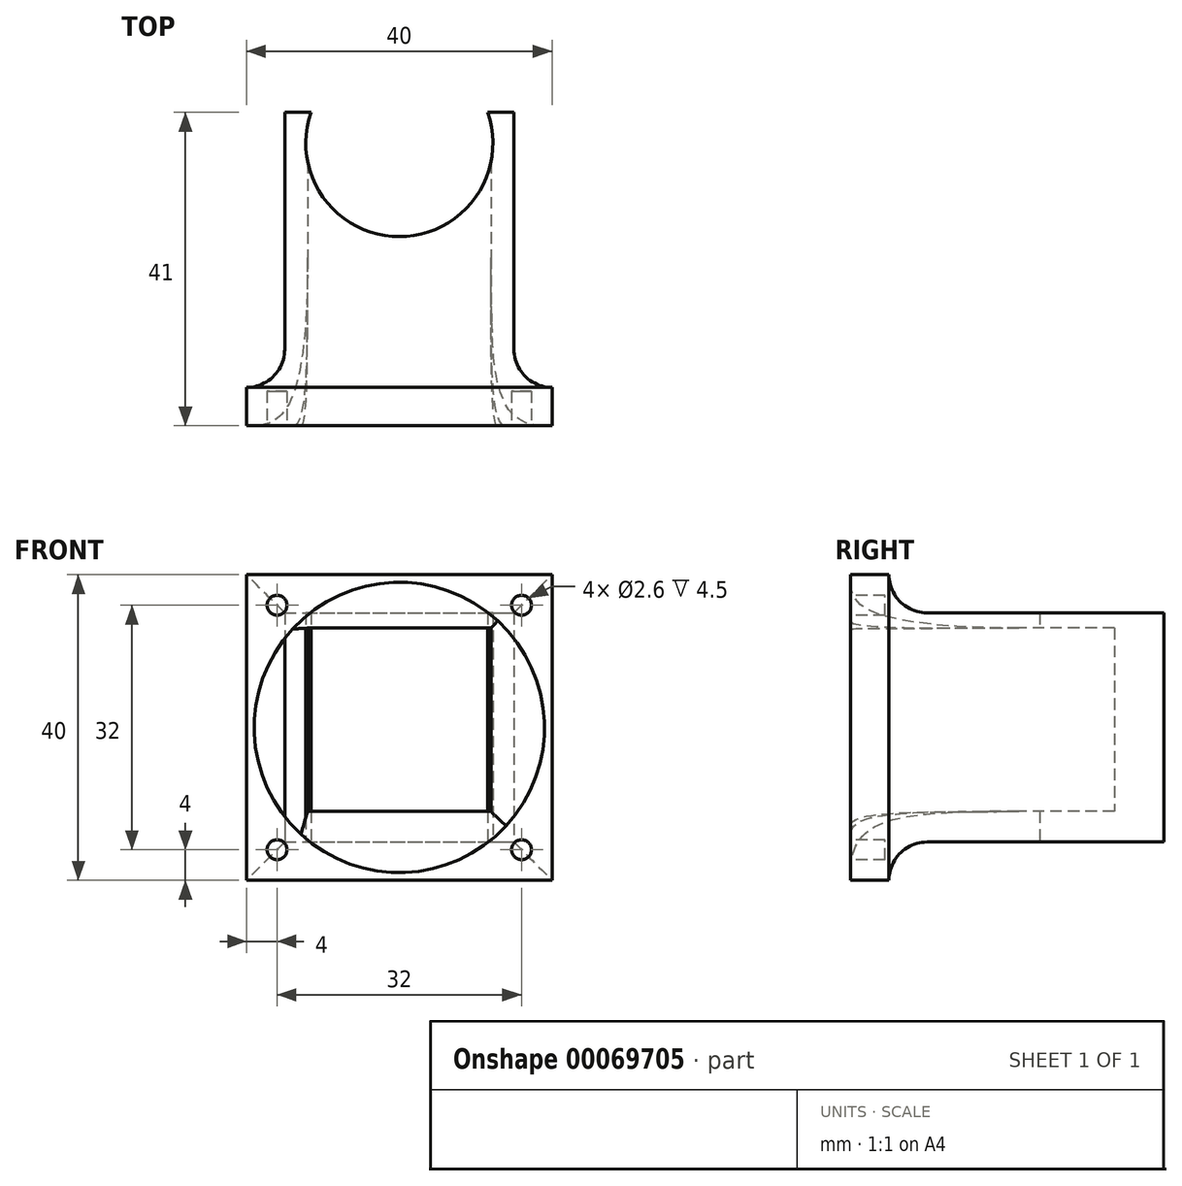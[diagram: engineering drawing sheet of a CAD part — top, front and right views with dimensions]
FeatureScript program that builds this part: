
annotation { "Feature Type Name" : "Feature", "Feature Type Description" : "" }
export const myFeature = defineFeature(function(context is Context, id is Id, definition is map)
    precondition{}
    {
        {
            var Q0;
            Q0=qCreatedBy(makeId("Top.planeOp"),FACE);
            var sketch = newSketch(context, id + "F0", { "sketchPlane" : qUnion([Q0])});
            skArc(sketch, "E0", {"start": v(-11.58, 4) * mm, "mid": v(0, -12.25) * mm, "end": v(11.58, 4) * mm});
            skLineSegment(sketch, "E1.bottom", {"start": v(-15, 4) * mm, "end": v(-11.58, 4) * mm});
            skLineSegment(sketch, "E1.left", {"start": v(-15, 4) * mm, "end": v(-15, -32) * mm});
            skLineSegment(sketch, "E1.right", {"start": v(15, 4) * mm, "end": v(15, -32) * mm});
            skLineSegment(sketch, "E2.bottom", {"start": v(-20, -32) * mm, "end": v(-15, -32) * mm});
            skLineSegment(sketch, "E2.top", {"start": v(-20, -37) * mm, "end": v(20, -37) * mm});
            skLineSegment(sketch, "E2.left", {"start": v(-20, -32) * mm, "end": v(-20, -37) * mm});
            skLineSegment(sketch, "E2.right", {"start": v(20, -32) * mm, "end": v(20, -37) * mm});
            skLineSegment(sketch, "E3.trimOffspring", {"start": v(15, -32) * mm, "end": v(20, -32) * mm});
            skLineSegment(sketch, "E4.trimOffspring", {"start": v(11.58, 4) * mm, "end": v(15, 4) * mm});
            skSolve(sketch);
        }
        {
            var Q0;
            Q0=makeQuery(id+"F0.imprint","IMPRINT",FACE,{"disambiguationData":[TD([[makeQuery(id+"F0.imprint","IMPRINT",EDGE,{"derivedFrom":sQuery(id+"F0.wireOp",EDGE,"E0")}),-1.0]])]});
            extrude(context, id + "F1", {"entities" : qUnion([Q0]), "depth" : 30 * mm, "offsetDistance" : 25 * mm});
        }
        {
            var Q0;
            Q0=makeQuery(id+"F1.opExtrude","CAP_FACE",FACE,{"disambiguationData":[OSD([sQuery(id+"F0.wireOp",EDGE,"E0"),sQuery(id+"F0.wireOp",EDGE,"E1.bottom"),sQuery(id+"F0.wireOp",EDGE,"E1.left"),sQuery(id+"F0.wireOp",EDGE,"E1.right"),sQuery(id+"F0.wireOp",EDGE,"E2.bottom"),sQuery(id+"F0.wireOp",EDGE,"E2.top"),sQuery(id+"F0.wireOp",EDGE,"E2.left"),sQuery(id+"F0.wireOp",EDGE,"E2.right"),sQuery(id+"F0.wireOp",EDGE,"E3.trimOffspring"),sQuery(id+"F0.wireOp",EDGE,"E4.trimOffspring")])],"isStart":true});
            var sketch = newSketch(context, id + "F2", { "sketchPlane" : qUnion([Q0])});
            skLineSegment(sketch, "E5.bottom", {"start": v(-20, 37) * mm, "end": v(20, 37) * mm});
            skLineSegment(sketch, "E5.top", {"start": v(-20, 32) * mm, "end": v(20, 32) * mm});
            skLineSegment(sketch, "E5.left", {"start": v(-20, 37) * mm, "end": v(-20, 32) * mm});
            skLineSegment(sketch, "E5.right", {"start": v(20, 37) * mm, "end": v(20, 32) * mm});
            skSolve(sketch);
        }
        {
            var Q0;
            Q0 = qSketchRegion(id + "F2", true);
            extrude(context, id + "F3", {"entities" : qUnion([Q0]), "operationType" : NewBodyOperationType.ADD, "depth" : 5 * mm, "offsetDistance" : 25 * mm, "hasSecondDirection" : true, "secondDirectionOppositeDirection" : true, "secondDirectionDepth" : 35 * mm});
        }
        {
            var Q0;
            Q0=makeQuery(id+"F3.boolean.opBoolean","MERGE",FACE,{"derivedFrom":[makeQuery(id+"F1.opExtrude","SWEPT_FACE",FACE,{"disambiguationData":[OSD([sQuery(id+"F0.wireOp",EDGE,"E2.top")])]}),makeQuery(id+"F3.opExtrude","SWEPT_FACE",FACE,{"disambiguationData":[OSD([sQuery(id+"F2.wireOp",EDGE,"E5.bottom")])]})]});
            var sketch = newSketch(context, id + "F4", { "sketchPlane" : qUnion([Q0])});
            skCircle(sketch, "E6", {"center": v(0, 15) * mm, "radius": 19 * mm});
            skPoint(sketch, "E6.centerSnap0", {"position": v(0, 35) * mm});
            skCircle(sketch, "E7", {"center": v(16, -1) * mm, "radius": 1.3 * mm});
            skCircle(sketch, "E8.0.1.0", {"center": v(16, 31) * mm, "radius": 1.3 * mm});
            skCircle(sketch, "E8.1.0.0", {"center": v(-16, -1) * mm, "radius": 1.3 * mm});
            skCircle(sketch, "E8.1.1.0", {"center": v(-16, 31) * mm, "radius": 1.3 * mm});
            skLineSegment(sketch, "E8.direction1", {"start": v(16, -1) * mm, "end": v(-16, -1) * mm, "construction": true});
            skLineSegment(sketch, "E8.direction2", {"start": v(16, -1) * mm, "end": v(16, 31) * mm, "construction": true});
            skSolve(sketch);
        }
        {
            var Q0;
            Q0=makeQuery(id+"F3.boolean.opBoolean","INTERSECT",EDGE,{"derivedFrom":[makeQuery(id+"F1.opExtrude","CAP_FACE",FACE,{"disambiguationData":[OSD([sQuery(id+"F0.wireOp",EDGE,"E0"),sQuery(id+"F0.wireOp",EDGE,"E1.bottom"),sQuery(id+"F0.wireOp",EDGE,"E1.left"),sQuery(id+"F0.wireOp",EDGE,"E1.right"),sQuery(id+"F0.wireOp",EDGE,"E2.bottom"),sQuery(id+"F0.wireOp",EDGE,"E2.top"),sQuery(id+"F0.wireOp",EDGE,"E2.left"),sQuery(id+"F0.wireOp",EDGE,"E2.right"),sQuery(id+"F0.wireOp",EDGE,"E3.trimOffspring"),sQuery(id+"F0.wireOp",EDGE,"E4.trimOffspring")])],"isStart":false}),makeQuery(id+"F3.opExtrude","SWEPT_FACE",FACE,{"disambiguationData":[OSD([sQuery(id+"F2.wireOp",EDGE,"E5.top")])]})]});
            var Q1;
            Q1=makeQuery(id+"F1.opExtrude","SWEPT_EDGE",EDGE,{"disambiguationData":[OSD([sQuery(id+"F0.wireOp",EDGE,"E1.right"),sQuery(id+"F0.wireOp",EDGE,"E3.trimOffspring")])]});
            var Q2;
            Q2=makeQuery(id+"F3.boolean.opBoolean","INTERSECT",EDGE,{"derivedFrom":[makeQuery(id+"F1.opExtrude","CAP_FACE",FACE,{"disambiguationData":[OSD([sQuery(id+"F0.wireOp",EDGE,"E0"),sQuery(id+"F0.wireOp",EDGE,"E1.bottom"),sQuery(id+"F0.wireOp",EDGE,"E1.left"),sQuery(id+"F0.wireOp",EDGE,"E1.right"),sQuery(id+"F0.wireOp",EDGE,"E2.bottom"),sQuery(id+"F0.wireOp",EDGE,"E2.top"),sQuery(id+"F0.wireOp",EDGE,"E2.left"),sQuery(id+"F0.wireOp",EDGE,"E2.right"),sQuery(id+"F0.wireOp",EDGE,"E3.trimOffspring"),sQuery(id+"F0.wireOp",EDGE,"E4.trimOffspring")])],"isStart":true}),makeQuery(id+"F3.opExtrude","SWEPT_FACE",FACE,{"disambiguationData":[OSD([sQuery(id+"F2.wireOp",EDGE,"E5.top")])]})]});
            var Q3;
            Q3=makeQuery(id+"F1.opExtrude","SWEPT_EDGE",EDGE,{"disambiguationData":[OSD([sQuery(id+"F0.wireOp",EDGE,"E1.left"),sQuery(id+"F0.wireOp",EDGE,"E2.bottom")])]});
            fillet(context, id + "F5", {"entities" : qUnion([Q0, Q1, Q2, Q3]), "radius" : 5 * mm, "tangentPropagation" : true, "allowEdgeOverflow" : false});
        }
        {
            var Q0;
            Q0=qCreatedBy(makeId("Front.planeOp"),FACE);
            cPlane(context, id + "F6", {"entities" : qUnion([Q0]), "cplaneType" : CPlaneType.OFFSET, "offset" : 15 * mm, "width" : 150 * mm, "height" : 150 * mm});
        }
        {
            var Q0;
            Q0=qCreatedBy(id+"F6.planeOp",FACE);
            var sketch = newSketch(context, id + "F7", { "sketchPlane" : qUnion([Q0])});
            skLineSegment(sketch, "E9.bottom", {"start": v(12, 28) * mm, "end": v(-12, 28) * mm});
            skLineSegment(sketch, "E9.top", {"start": v(12, 4) * mm, "end": v(-12, 4) * mm});
            skLineSegment(sketch, "E9.left", {"start": v(12, 28) * mm, "end": v(12, 4) * mm});
            skLineSegment(sketch, "E9.right", {"start": v(-12, 28) * mm, "end": v(-12, 4) * mm});
            skSolve(sketch);
        }
        {
            var Q1;
            Q1=makeQuery(id+"F4.imprint","IMPRINT",FACE,{"disambiguationData":[TD([[makeQuery(id+"F4.imprint","IMPRINT",EDGE,{"derivedFrom":sQuery(id+"F4.wireOp",EDGE,"E6")}),1.0]])]});
            var Q2;
            Q2=makeQuery(id+"F7.imprint","IMPRINT",FACE,{"disambiguationData":[TD([[makeQuery(id+"F7.imprint","IMPRINT",EDGE,{"derivedFrom":sQuery(id+"F7.wireOp",EDGE,"E9.bottom")}),1.0]])]});
            loft(context, id + "F8", {"operationType" : NewBodyOperationType.REMOVE, "startCondition" : LoftEndDerivativeType.TANGENT_TO_PROFILE, "startMagnitude" : 3, "endCondition" : LoftEndDerivativeType.NORMAL_TO_PROFILE, "endMagnitude" : 2, "sheetProfilesArray" : [{ "sheetProfileEntities" : qUnion([Q1]) }, { "sheetProfileEntities" : qUnion([Q2]) }]});
        }
        {
            var Q0;
            Q0=qCreatedBy(makeId("Front.planeOp"),FACE);
            cPlane(context, id + "F9", {"entities" : qUnion([Q0]), "cplaneType" : CPlaneType.OFFSET, "offset" : 10 * mm, "width" : 150 * mm, "height" : 150 * mm});
        }
        {
            var Q0;
            Q0=makeQuery(id+"F7.imprint","IMPRINT",FACE,{"disambiguationData":[TD([[makeQuery(id+"F7.imprint","IMPRINT",EDGE,{"derivedFrom":sQuery(id+"F7.wireOp",EDGE,"E9.bottom")}),1.0]])]});
            extrude(context, id + "F10", {"entities" : qUnion([Q0]), "operationType" : NewBodyOperationType.REMOVE, "oppositeDirection" : true, "depth" : 14 * mm, "offsetDistance" : 25 * mm});
        }
        {
            var Q0;
            Q0=makeQuery(id+"F4.imprint","IMPRINT",FACE,{"disambiguationData":[TD([[makeQuery(id+"F4.imprint","IMPRINT",EDGE,{"derivedFrom":sQuery(id+"F4.wireOp",EDGE,"E7")}),1.0]])]});
            var Q1;
            Q1=makeQuery(id+"F4.imprint","IMPRINT",FACE,{"disambiguationData":[TD([[makeQuery(id+"F4.imprint","IMPRINT",EDGE,{"derivedFrom":sQuery(id+"F4.wireOp",EDGE,"E8.1.0.0")}),1.0]])]});
            var Q2;
            Q2=makeQuery(id+"F4.imprint","IMPRINT",FACE,{"disambiguationData":[TD([[makeQuery(id+"F4.imprint","IMPRINT",EDGE,{"derivedFrom":sQuery(id+"F4.wireOp",EDGE,"E8.1.1.0")}),1.0]])]});
            var Q3;
            Q3=makeQuery(id+"F4.imprint","IMPRINT",FACE,{"disambiguationData":[TD([[makeQuery(id+"F4.imprint","IMPRINT",EDGE,{"derivedFrom":sQuery(id+"F4.wireOp",EDGE,"E8.0.1.0")}),1.0]])]});
            extrude(context, id + "F11", {"entities" : qUnion([Q0, Q1, Q2, Q3]), "operationType" : NewBodyOperationType.REMOVE, "oppositeDirection" : true, "depth" : 4.5 * mm, "offsetDistance" : 25 * mm});
        }
    });
